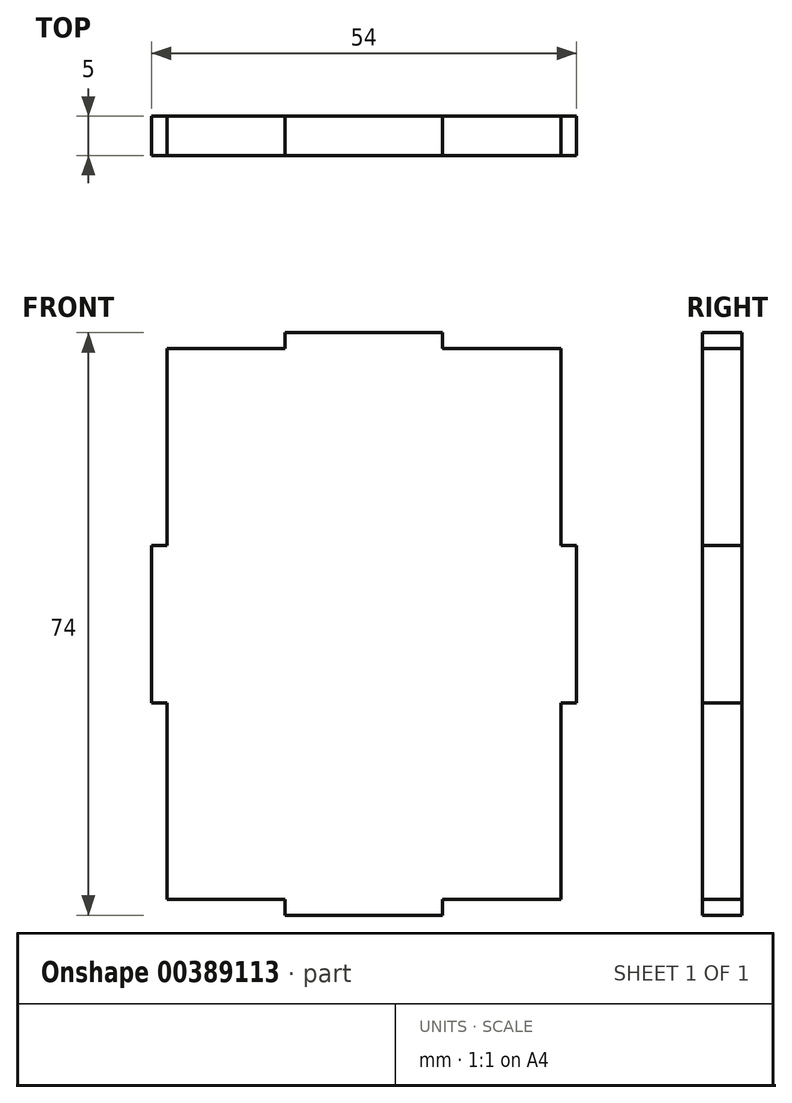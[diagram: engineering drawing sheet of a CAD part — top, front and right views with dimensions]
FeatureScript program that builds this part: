
annotation { "Feature Type Name" : "Feature", "Feature Type Description" : "" }
export const myFeature = defineFeature(function(context is Context, id is Id, definition is map)
    precondition{}
    {
        {
            var Q0;
            Q0=qCreatedBy(makeId("Front.planeOp"),FACE);
            var sketch = newSketch(context, id + "F0", { "sketchPlane" : qUnion([Q0])});
            skLineSegment(sketch, "E0", {"start": v(0, 0) * mm, "end": v(0, 25) * mm});
            skLineSegment(sketch, "E1", {"start": v(0, 25) * mm, "end": v(-2, 25) * mm});
            skLineSegment(sketch, "E2", {"start": v(-2, 25) * mm, "end": v(-2, 45) * mm});
            skLineSegment(sketch, "E3", {"start": v(-2, 45) * mm, "end": v(0, 45) * mm});
            skLineSegment(sketch, "E4", {"start": v(0, 45) * mm, "end": v(0, 70) * mm});
            skLineSegment(sketch, "E5", {"start": v(0, 70) * mm, "end": v(15, 70) * mm});
            skLineSegment(sketch, "E6", {"start": v(15, 70) * mm, "end": v(15, 72) * mm});
            skLineSegment(sketch, "E7", {"start": v(15, 72) * mm, "end": v(35, 72) * mm});
            skLineSegment(sketch, "E8", {"start": v(35, 72) * mm, "end": v(35, 70) * mm});
            skLineSegment(sketch, "E9", {"start": v(35, 70) * mm, "end": v(50, 70) * mm});
            skLineSegment(sketch, "E10", {"start": v(50, 70) * mm, "end": v(50, 45) * mm});
            skLineSegment(sketch, "E11", {"start": v(50, 45) * mm, "end": v(52, 45) * mm});
            skLineSegment(sketch, "E12", {"start": v(52, 45) * mm, "end": v(52, 25) * mm});
            skLineSegment(sketch, "E13", {"start": v(52, 25) * mm, "end": v(50, 25) * mm});
            skLineSegment(sketch, "E14", {"start": v(50, 25) * mm, "end": v(50, 0) * mm});
            skLineSegment(sketch, "E15", {"start": v(50, 0) * mm, "end": v(35, 0) * mm});
            skLineSegment(sketch, "E16", {"start": v(35, 0) * mm, "end": v(35, -2) * mm});
            skLineSegment(sketch, "E17", {"start": v(35, -2) * mm, "end": v(15, -2) * mm});
            skLineSegment(sketch, "E18", {"start": v(15, -2) * mm, "end": v(15, 0) * mm});
            skLineSegment(sketch, "E19", {"start": v(15, 0) * mm, "end": v(0, 0) * mm});
            skSolve(sketch);
        }
        {
            var Q0;
            Q0=makeQuery(id+"F0.imprint","IMPRINT",FACE,{"disambiguationData":[TD([[makeQuery(id+"F0.imprint","IMPRINT",EDGE,{"derivedFrom":sQuery(id+"F0.wireOp",EDGE,"E0")}),-1.0]])]});
            extrude(context, id + "F1", {"entities" : qUnion([Q0]), "depth" : 5 * mm});
        }
    });
